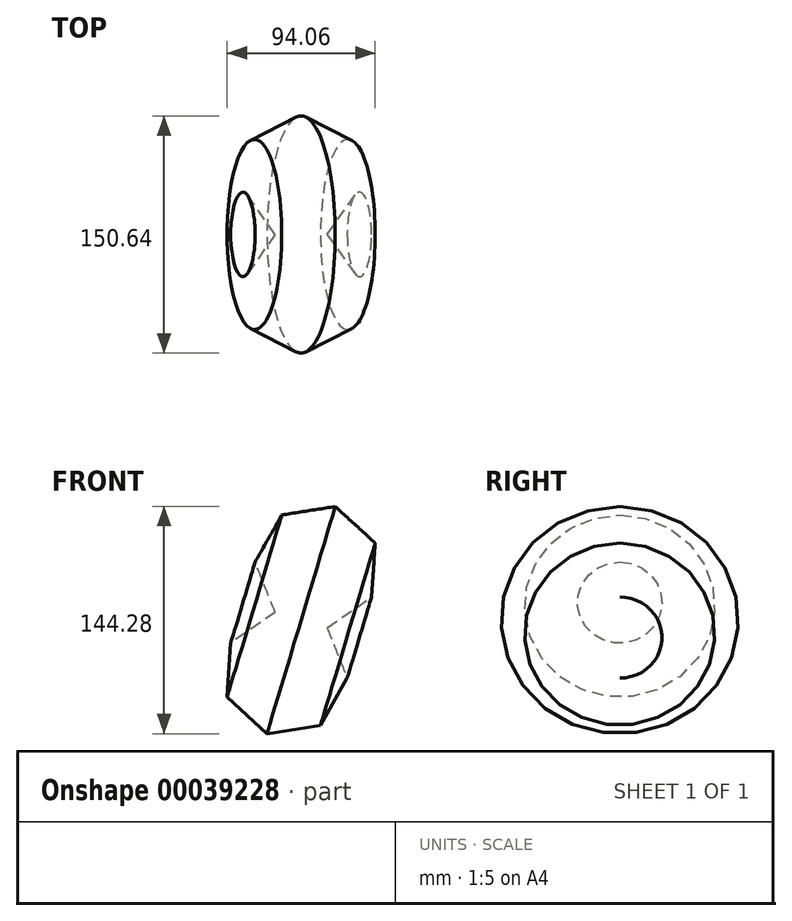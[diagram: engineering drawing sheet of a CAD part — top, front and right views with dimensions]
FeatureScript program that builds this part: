
annotation { "Feature Type Name" : "Feature", "Feature Type Description" : "" }
export const myFeature = defineFeature(function(context is Context, id is Id, definition is map)
    precondition{}
    {
        {
            var Q0;
            Q0=qCreatedBy(makeId("Front.planeOp"),FACE);
            var sketch = newSketch(context, id + "F0", { "sketchPlane" : qUnion([Q0])});
            skCircle(sketch, "E0.cCircle", {"center": v(0, 0) * mm, "radius": 35.7 * mm, "construction": true});
            skLineSegment(sketch, "E0.0", {"start": v(22.57, -32.56) * mm, "end": v(-11.39, -37.95) * mm});
            skLineSegment(sketch, "E0.1", {"start": v(-11.39, -37.95) * mm, "end": v(-36.77, -14.76) * mm});
            skLineSegment(sketch, "E0.2", {"start": v(-36.77, -14.76) * mm, "end": v(-34.46, 19.55) * mm});
            skLineSegment(sketch, "E0.3", {"start": v(-34.46, 19.55) * mm, "end": v(-6.2, 39.13) * mm});
            skLineSegment(sketch, "E0.4", {"start": v(-6.2, 39.13) * mm, "end": v(26.72, 29.25) * mm});
            skLineSegment(sketch, "E0.5", {"start": v(26.72, 29.25) * mm, "end": v(39.53, -2.66) * mm});
            skLineSegment(sketch, "E0.6", {"start": v(39.53, -2.66) * mm, "end": v(22.57, -32.56) * mm});
            skPoint(sketch, "E0.0.midPoint", {"position": v(5.6, -35.26) * mm});
            skCircle(sketch, "E1", {"center": v(0, 0) * mm, "radius": 27.2 * mm});
            skSolve(sketch);
        }
        {
            var Q0;
            Q0=makeQuery(id+"F0.imprint","IMPRINT",FACE,{"disambiguationData":[TD([[makeQuery(id+"F0.imprint","IMPRINT",EDGE,{"derivedFrom":sQuery(id+"F0.wireOp",EDGE,"E1")}),1.0]])]});
            var Q1;
            Q1=makeQuery(id+"F0.imprint","IMPRINT",FACE,{"disambiguationData":[TD([[makeQuery(id+"F0.imprint","IMPRINT",EDGE,{"derivedFrom":sQuery(id+"F0.wireOp",EDGE,"E0.0")}),-1.0]])]});
            var Q2;
            Q2=sQuery(id+"F0.wireOp",EDGE,"E0.4");
            revolve(context, id + "F1", {"entities" : qUnion([Q0, Q1]), "axis" : qUnion([Q2]), "revolveType" : RevolveType.FULL});
        }
    });
